# Revit family: Dartmouth Twin GU 10
name_source: partatom
category: Lighting Fixtures
revit_build: Autodesk Revit 2018 (Build: 20170223_1515(x64)
units: mm (PartAtom-declared; Revit-internal decimal feet)

## family parameters
Always vertical = Yes
Cut with Voids When Loaded = No
Host = Wall
Light Source = No
OmniClass Number = 23.80.70.00
OmniClass Title = Lighting
Part Type = Normal
Room Calculation Point = No
Round Connector Dimension = Use Diameter
Shared = No

## types (3) — shared parameters
Dimensions MM = 165 x 65 x 102
Dimmable = Lamp Dependent
Dimming Method = Lamp Dependent
Driver Required = No
Efficacy (lm/w) = Lamp Dependent
Electrical Class = 1
Lamp = 2 X GU10
Light Source Fixed = yes
Location rating = IP54
Main Material = Metal - Aluminium
Manufacturer = Astro Lighting Ltd
Power (Watts) = 6 W Max
Product Location = outdoor, Zone 2, 3
Product Name = Dartmouth Twin
Product URL = https://www.astrolighting.com
URL = www.astrolighting.com
Wattage Comments = 6 W
Weight KG = 1 mm  [stored 0.00328084 ft]

## per-type parameters (varying)
| type | Main Finish | Product SKU |
| Astro Dartmouth Twin Textured Black | Textured Black | 1372014 |
| Astro Dartmouth Twin Textured Grey | Textured Grey | 1372013 |
| Astro Dartmouth Twin Textured White | Textured White | 1372012 |

note: [stored X ft] marks values corroborated as IEEE doubles in the binary element streams (Revit-internal decimal feet)

## geometry (parser evidence)
native form markers: Sweep x2
no freeform markers — native parametric forms only
